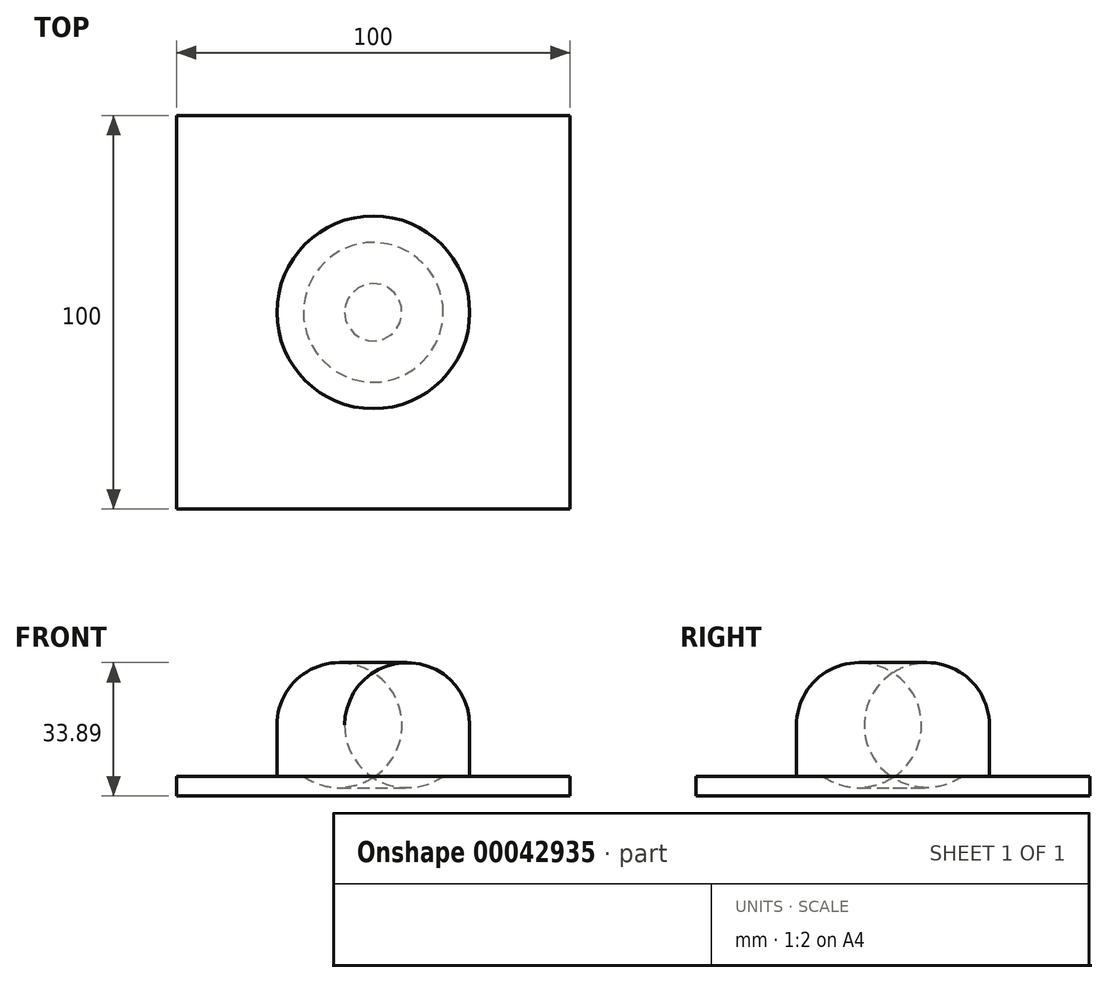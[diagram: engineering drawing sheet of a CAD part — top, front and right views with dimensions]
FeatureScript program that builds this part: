
annotation { "Feature Type Name" : "Feature", "Feature Type Description" : "" }
export const myFeature = defineFeature(function(context is Context, id is Id, definition is map)
    precondition{}
    {
        {
            var Q0;
            Q0=qCreatedBy(makeId("Front.planeOp"),FACE);
            var sketch = newSketch(context, id + "F0", { "sketchPlane" : qUnion([Q0])});
            skLineSegment(sketch, "E0.bottom", {"start": v(0, 0) * mm, "end": v(-50, 0) * mm});
            skLineSegment(sketch, "E0.top", {"start": v(0, -5) * mm, "end": v(-50, -5) * mm});
            skLineSegment(sketch, "E0.left", {"start": v(0, 0) * mm, "end": v(0, -5) * mm});
            skLineSegment(sketch, "E0.right", {"start": v(-50, 0) * mm, "end": v(-50, -5) * mm});
            skLineSegment(sketch, "E1.bottom", {"start": v(0, 0) * mm, "end": v(-24.5, 0) * mm});
            skLineSegment(sketch, "E1.right", {"start": v(-24.5, 0) * mm, "end": v(-24.5, 13) * mm});
            skLineSegment(sketch, "E2.MirrorCS", {"start": v(0, 0) * mm, "end": v(50, 0) * mm});
            skLineSegment(sketch, "E3.MirrorCS", {"start": v(50, 0) * mm, "end": v(50, -5) * mm});
            skLineSegment(sketch, "E4.MirrorCS", {"start": v(0, -5) * mm, "end": v(50, -5) * mm});
            skArc(sketch, "E5", {"start": v(-24.5, 13) * mm, "mid": v(-22.71, 5.68) * mm, "end": v(-17.75, 0) * mm});
            skLineSegment(sketch, "E6.bottom", {"start": v(-24.5, 0) * mm, "end": v(-29.5, 0) * mm});
            skLineSegment(sketch, "E6.top", {"start": v(-24.5, 30) * mm, "end": v(-29.5, 30) * mm});
            skLineSegment(sketch, "E6.left", {"start": v(-24.5, 0) * mm, "end": v(-24.5, 30) * mm});
            skLineSegment(sketch, "E6.right", {"start": v(-29.5, 0) * mm, "end": v(-29.5, 30) * mm});
            skSolve(sketch);
        }
        {
            var Q0;
            {var subQ0=sQuery(id+"F0.wireOp",EDGE,"E6.bottom");Q0=makeQuery(id+"F0.imprint","IMPRINT",FACE,{"disambiguationData":[TD([[makeQuery(id+"F0.imprint","IMPRINT",EDGE,{"derivedFrom":subQ0}),-1.0]])]});}
            var Q1;
            {var subQ1=sQuery(id+"F0.wireOp",EDGE,"E5");Q1=makeQuery(id+"F0.imprint","IMPRINT",FACE,{"disambiguationData":[TD([[makeQuery(id+"F0.imprint","IMPRINT",EDGE,{"derivedFrom":subQ1}),-1.0]])]});}
            var Q2;
            Q2=sQuery(id+"F0.wireOp",EDGE,"E0.left");
            revolve(context, id + "F1", {"entities" : qUnion([Q0, Q1]), "axis" : qUnion([Q2]), "revolveType" : RevolveType.FULL});
        }
        {
            var Q0;
            Q0=makeQuery(id+"F0.imprint","IMPRINT",FACE,{"disambiguationData":[TD([[makeQuery(id+"F0.imprint","IMPRINT",EDGE,{"derivedFrom":sQuery(id+"F0.wireOp",EDGE,"E0.bottom")}),1.0]])]});
            var Q1;
            Q1=makeQuery(id+"F0.imprint","IMPRINT",FACE,{"disambiguationData":[TD([[makeQuery(id+"F0.imprint","IMPRINT",EDGE,{"derivedFrom":sQuery(id+"F0.wireOp",EDGE,"E0.left")}),1.0]])]});
            extrude(context, id + "F2", {"entities" : qUnion([Q0, Q1]), "operationType" : NewBodyOperationType.ADD, "endBound" : BoundingType.SYMMETRIC, "depth" : 100 * mm});
        }
        {
            var Q0;
            Q0=makeQuery(id+"F1.opRevolve","SWEPT_BODY",BODY,{"disambiguationData":[OSD([sQuery(id+"F0.wireOp",EDGE,"E1.bottom"),sQuery(id+"F0.wireOp",EDGE,"E5"),sQuery(id+"F0.wireOp",EDGE,"E6.bottom"),sQuery(id+"F0.wireOp",EDGE,"E6.top"),sQuery(id+"F0.wireOp",EDGE,"E6.left"),sQuery(id+"F0.wireOp",EDGE,"E6.right")])]});
            transform(context, id + "F3", {"entities" : qUnion([Q0]), "transformType" : TransformType.TRANSLATION_3D, "dx" : 0 * mm, "dy" : 0 * mm, "dz" : 0 * mm, "makeCopy" : true});
        }
        {
            var Q0;
            Q0=makeQuery(id+"F3.opPattern","COPY",BODY,{"derivedFrom":makeQuery(id+"F1.opRevolve","SWEPT_BODY",BODY,{"disambiguationData":[OSD([sQuery(id+"F0.wireOp",EDGE,"E1.bottom"),sQuery(id+"F0.wireOp",EDGE,"E5"),sQuery(id+"F0.wireOp",EDGE,"E6.bottom"),sQuery(id+"F0.wireOp",EDGE,"E6.top"),sQuery(id+"F0.wireOp",EDGE,"E6.left"),sQuery(id+"F0.wireOp",EDGE,"E6.right")])]}),"instanceName":"1"});
            deleteBodies(context, id + "F4", {"entities" : qUnion([Q0])});
        }
    });
